# Revit family: kawneer-350ir_entrance 01_17319
name_source: partatom
category: Doors
revit_build: Autodesk Revit 2015 (Build: 20140905_0730(x64)
units: mm (PartAtom-declared; Revit-internal decimal feet)

## types (2) — shared parameters
Function = Interior
Glazing Finish = Glass
Height = 7' - 0"
Product data url = https://bimobject.com
Wall Closure = By host

## per-type parameters (varying)
| type | Assembly Code | Description | Frame Finish | Horizontal Frame Length | INSET | Manufacturer | Model | Rough Height | Rough Width | Transom Height | Type Comments | URL | Width |
| (2)3'-0"W X 7'-0"H W 1'4 TRANS | B2030210 | Standard entrances that provide the extra strength for applications where more stringent code requirements include windborne debris protection. | Default | 6' - 0" | 0' - 2" | Kawneer | 350 IR WITH IR 501 ENTRANCE FRAMING | 8' - 4" | 6' - 5" | 1' - 4" | 350 IR DOORS WITH IR 501 ENTRANCE FRAMING Hurricane Resistant (1-5/16" INFILL) | http://www.kawneer.com | 3' - 0" |
| (2)3'-0"W X 8'H W 2'TRANS |  |  | <By Category> | -0' - 5" | 0' - 1" |  |  | 8' - 5" | 0' - 0" | 1' - 5" |  |  | -0' - 2 1/2" |

## geometry (parser evidence)
native form markers: Sweep x29
no freeform markers — native parametric forms only
